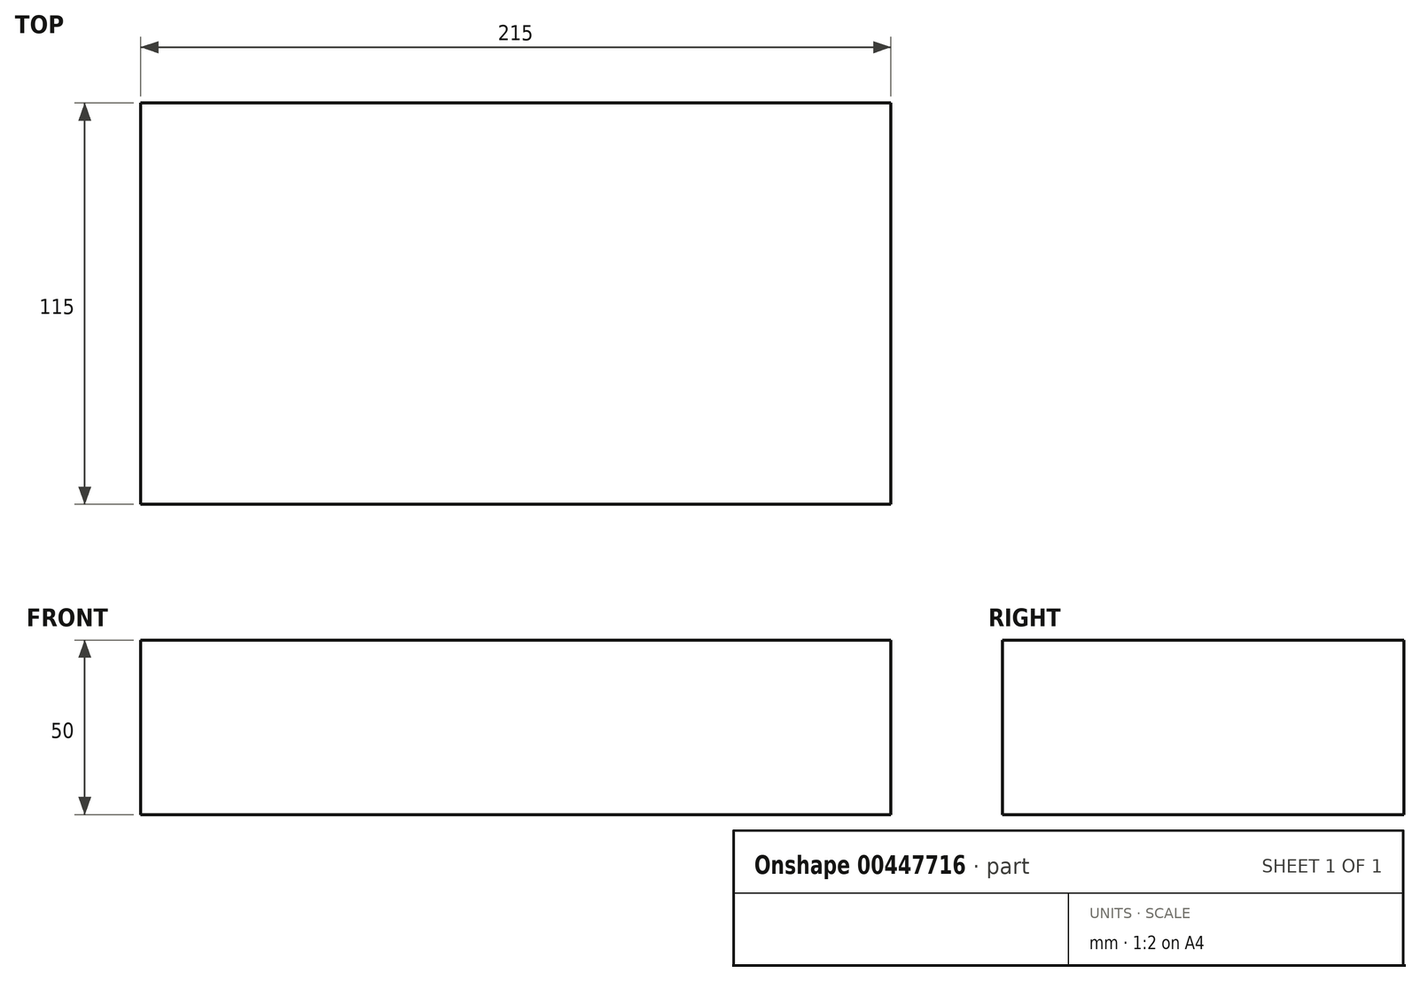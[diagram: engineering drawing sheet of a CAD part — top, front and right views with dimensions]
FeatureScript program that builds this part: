
annotation { "Feature Type Name" : "Feature", "Feature Type Description" : "" }
export const myFeature = defineFeature(function(context is Context, id is Id, definition is map)
    precondition{}
    {
        {
            var Q0;
            Q0=qCreatedBy(makeId("Top.planeOp"),FACE);
            var sketch = newSketch(context, id + "F0", { "sketchPlane" : qUnion([Q0])});
            skLineSegment(sketch, "E0.bottom", {"start": v(-104, 52.2) * mm, "end": v(111, 52.2) * mm});
            skLineSegment(sketch, "E0.top", {"start": v(-104, -62.8) * mm, "end": v(111, -62.8) * mm});
            skLineSegment(sketch, "E0.left", {"start": v(-104, 52.2) * mm, "end": v(-104, -62.8) * mm});
            skLineSegment(sketch, "E0.right", {"start": v(111, 52.2) * mm, "end": v(111, -62.8) * mm});
            skSolve(sketch);
        }
        {
            var Q0;
            Q0=makeQuery(id+"F0.imprint","IMPRINT",FACE,{"disambiguationData":[TD([[makeQuery(id+"F0.imprint","IMPRINT",EDGE,{"derivedFrom":sQuery(id+"F0.wireOp",EDGE,"E0.bottom")}),-1.0]])]});
            extrude(context, id + "F1", {"entities" : qUnion([Q0]), "depth" : 50 * mm});
        }
    });
